# Revit family: Dumbwaiter_RES_NationwideLifts_Jeeves-EconoLift
name_source: partatom
category: Generic Models
units: mm (PartAtom-declared; Revit-internal decimal feet)

## family parameters
Can host rebar = No
Classification Number = 23.50.30.11
Cut with Voids When Loaded = No
Host = Face
Maintain Annotation Orientation = No
Part Type = Normal
Room Calculation Point = No
Round Connector Dimension = Use Diameter
Shared = No

## types (8) — shared parameters
Assembly Code = D1010100
Default Elevation = 0' - 0"
Description = Nationwide Lifts Residential Dumbwaiter - Jeeves EconoLift as Specified
Keynote = 14 20 00
Lift Travel Speed = 30 fpm
Manufacturer = Nationwide Lifts, Inc.
Manufacturer Website = http://www.elevators.com
Maximum Size = 3 Stops and 35 ft of Travel
Model = Jeeves EconoLift
Product Data = http://www.arcat.com
Revision = R1_2016-05
Sales Information = http://www.elevators.com
Specification = http://www.arcat.com
Standards Conformance = ASME A17.1
URL = http://www.elevators.com
Unit Height = 2' - 6"
zero-valued in all types: Expected Lifespan (Years), Maintenance Schedule (Months), Warranty Duration (Years)

## per-type parameters (varying)
| type | Capacity | Opening Depth | Opening Width | Unit Depth | Unit Width |
| 24 x 24 x 30 150 lb Opposite Side Doors | 150 lbs | 2' - 4" | 2' - 7 1/2" | 2' - 0" | 2' - 0" |
| 24 x 24 x 30 100 lb Opposite Side Doors | 100 lbs | 2' - 4" | 2' - 7 1/2" | 2' - 0" | 2' - 0" |
| 20 x 20 x 30 150 lb Opposite Side Doors | 150 lbs | 2' - 0" | 2' - 3 1/2" | 1' - 8" | 1' - 8" |
| 20 x 20 x 30 100 lb Opposite Side Doors | 100 lbs | 2' - 0" | 2' - 3 1/2" | 1' - 8" | 1' - 8" |
| 24 x 24 x 30 150 lb Same Side Doors | 150 lbs | 2' - 4" | 2' - 7 1/2" | 2' - 0" | 2' - 0" |
| 24 x 24 x 30 100 lb Same Side Doors | 100 lbs | 2' - 4" | 2' - 7 1/2" | 2' - 0" | 2' - 0" |
| 20 x 20 x 30 150 lb Same Side Doors | 150 lbs | 2' - 0" | 2' - 3 1/2" | 1' - 8" | 1' - 8" |
| 20 x 20 x 30 100 lb Same Side Doors | 100 lbs | 2' - 0" | 2' - 3 1/2" | 1' - 8" | 1' - 8" |

## geometry (parser evidence)
native form markers: Sweep x2
no freeform markers — native parametric forms only
